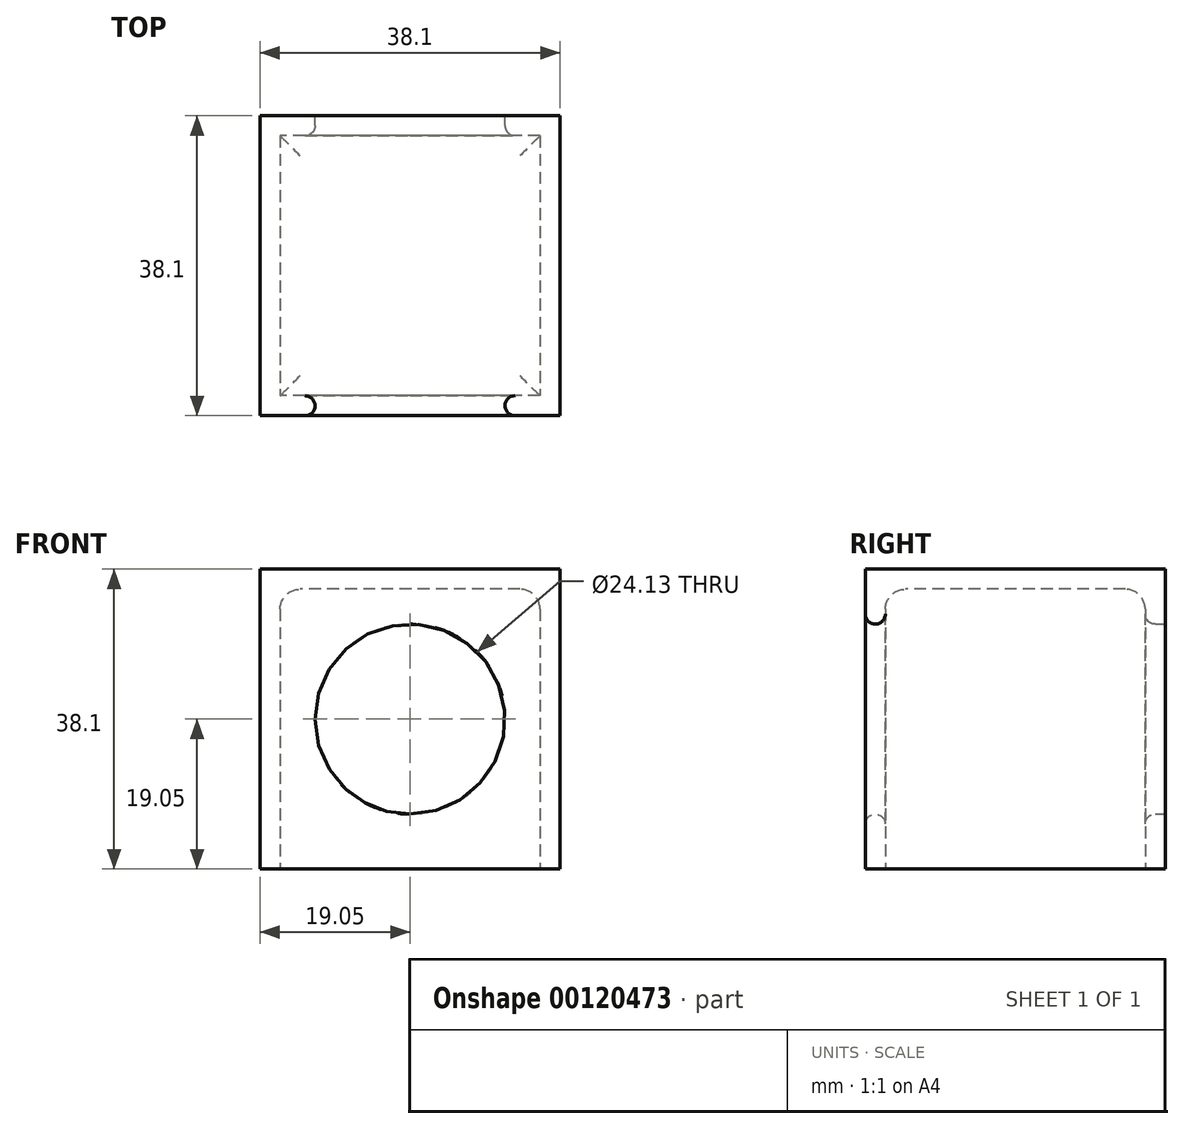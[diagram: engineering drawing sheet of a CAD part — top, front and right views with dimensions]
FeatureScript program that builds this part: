
annotation { "Feature Type Name" : "Feature", "Feature Type Description" : "" }
export const myFeature = defineFeature(function(context is Context, id is Id, definition is map)
    precondition{}
    {
        {
            var Q0;
            Q0=qCreatedBy(makeId("Top.planeOp"),FACE);
            var sketch = newSketch(context, id + "F0", { "sketchPlane" : qUnion([Q0])});
            skLineSegment(sketch, "E0.bottom", {"start": v(0, 0) * mm, "end": v(38.1, 0) * mm});
            skLineSegment(sketch, "E0.top", {"start": v(0, -38.1) * mm, "end": v(38.1, -38.1) * mm});
            skLineSegment(sketch, "E0.left", {"start": v(0, 0) * mm, "end": v(0, -38.1) * mm});
            skLineSegment(sketch, "E0.right", {"start": v(38.1, 0) * mm, "end": v(38.1, -38.1) * mm});
            skSolve(sketch);
        }
        {
            var Q0;
            Q0=makeQuery(id+"F0.imprint","IMPRINT",FACE,{"disambiguationData":[TD([[makeQuery(id+"F0.imprint","IMPRINT",EDGE,{"derivedFrom":sQuery(id+"F0.wireOp",EDGE,"E0.bottom")}),-1.0]])]});
            extrude(context, id + "F1", {"entities" : qUnion([Q0]), "depth" : 38.1 * mm});
        }
        {
            var Q0;
            Q0=makeQuery(id+"F1.opExtrude","CAP_FACE",FACE,{"disambiguationData":[OSD([sQuery(id+"F0.wireOp",EDGE,"E0.bottom"),sQuery(id+"F0.wireOp",EDGE,"E0.top"),sQuery(id+"F0.wireOp",EDGE,"E0.left"),sQuery(id+"F0.wireOp",EDGE,"E0.right")])],"isStart":true});
            var sketch = newSketch(context, id + "F2", { "sketchPlane" : qUnion([Q0])});
            skLineSegment(sketch, "E1.bottom", {"start": v(38.1, 0) * mm, "end": v(35.56, 0) * mm});
            skLineSegment(sketch, "E1.top", {"start": v(38.1, 2.54) * mm, "end": v(35.56, 2.54) * mm});
            skLineSegment(sketch, "E1.left", {"start": v(38.1, 0) * mm, "end": v(38.1, 2.54) * mm});
            skLineSegment(sketch, "E1.right", {"start": v(35.56, 0) * mm, "end": v(35.56, 2.54) * mm});
            skLineSegment(sketch, "E2.bottom", {"start": v(35.56, 2.54) * mm, "end": v(2.54, 2.54) * mm});
            skLineSegment(sketch, "E2.top", {"start": v(35.56, 35.56) * mm, "end": v(2.54, 35.56) * mm});
            skLineSegment(sketch, "E2.left", {"start": v(35.56, 2.54) * mm, "end": v(35.56, 35.56) * mm});
            skLineSegment(sketch, "E2.right", {"start": v(2.54, 2.54) * mm, "end": v(2.54, 35.56) * mm});
            skSolve(sketch);
        }
        {
            var Q0;
            Q0=makeQuery(id+"F2.imprint","IMPRINT",FACE,{"disambiguationData":[TD([[makeQuery(id+"F2.imprint","IMPRINT",EDGE,{"derivedFrom":sQuery(id+"F2.wireOp",EDGE,"E2.bottom")}),-1.0]])]});
            extrude(context, id + "F3", {"entities" : qUnion([Q0]), "operationType" : NewBodyOperationType.REMOVE, "oppositeDirection" : true, "depth" : 35.56 * mm});
        }
        {
            var Q0;
            Q0=makeQuery(id+"F3.boolean.opBoolean","COPY",EDGE,{"derivedFrom":makeQuery(id+"F3.opExtrude","CAP_EDGE",EDGE,{"disambiguationData":[OSD([sQuery(id+"F2.wireOp",EDGE,"E2.top")])],"isStart":false})});
            var Q1;
            Q1=makeQuery(id+"F3.boolean.opBoolean","COPY",EDGE,{"derivedFrom":makeQuery(id+"F3.opExtrude","CAP_EDGE",EDGE,{"disambiguationData":[OSD([sQuery(id+"F2.wireOp",EDGE,"E2.right")])],"isStart":false})});
            var Q2;
            Q2=makeQuery(id+"F3.boolean.opBoolean","COPY",EDGE,{"derivedFrom":makeQuery(id+"F3.opExtrude","CAP_EDGE",EDGE,{"disambiguationData":[OSD([sQuery(id+"F2.wireOp",EDGE,"E2.left")])],"isStart":false})});
            var Q3;
            Q3=makeQuery(id+"F3.boolean.opBoolean","COPY",EDGE,{"derivedFrom":makeQuery(id+"F3.opExtrude","CAP_EDGE",EDGE,{"disambiguationData":[OSD([sQuery(id+"F2.wireOp",EDGE,"E2.bottom")])],"isStart":false})});
            fillet(context, id + "F4", {"entities" : qUnion([Q0, Q1, Q2, Q3]), "radius" : 2.54 * mm, "tangentPropagation" : true, "allowEdgeOverflow" : false});
        }
        {
            var Q0;
            Q0=makeQuery(id+"F1.opExtrude","SWEPT_FACE",FACE,{"disambiguationData":[OSD([sQuery(id+"F0.wireOp",EDGE,"E0.bottom")])]});
            var sketch = newSketch(context, id + "F5", { "sketchPlane" : qUnion([Q0])});
            skCircle(sketch, "E3", {"center": v(-19.05, 19.05) * mm, "radius": 12.07 * mm});
            skSolve(sketch);
        }
        {
            var Q0;
            Q0 = qSketchRegion(id + "F5", true);
            extrude(context, id + "F6", {"entities" : qUnion([Q0]), "operationType" : NewBodyOperationType.REMOVE, "endBound" : BoundingType.THROUGH_ALL, "oppositeDirection" : true, "depth" : 25.4 * mm});
        }
        {
            var Q0;
            Q0=makeQuery(id+"F6.boolean.opBoolean","COPY",EDGE,{"derivedFrom":makeQuery(id+"F6.opExtrude","CAP_EDGE",EDGE,{"disambiguationData":[OSD([sQuery(id+"F5.wireOp",EDGE,"E3")])],"isStart":true})});
            var Q1;
            Q1=makeQuery(id+"F6.boolean.opBoolean","INTERSECT",EDGE,{"derivedFrom":[makeQuery(id+"F3.boolean.opBoolean","COPY",FACE,{"derivedFrom":makeQuery(id+"F3.opExtrude","SWEPT_FACE",FACE,{"disambiguationData":[OSD([sQuery(id+"F2.wireOp",EDGE,"E2.bottom")])]})}),makeQuery(id+"F6.opExtrude","SWEPT_FACE",FACE,{"disambiguationData":[OSD([sQuery(id+"F5.wireOp",EDGE,"E3")])]})]});
            var Q2;
            Q2=makeQuery(id+"F6.boolean.opBoolean","INTERSECT",EDGE,{"derivedFrom":[makeQuery(id+"F3.boolean.opBoolean","COPY",FACE,{"derivedFrom":makeQuery(id+"F3.opExtrude","SWEPT_FACE",FACE,{"disambiguationData":[OSD([sQuery(id+"F2.wireOp",EDGE,"E2.top")])]})}),makeQuery(id+"F6.opExtrude","SWEPT_FACE",FACE,{"disambiguationData":[OSD([sQuery(id+"F5.wireOp",EDGE,"E3")])]})]});
            var Q3;
            Q3=makeQuery(id+"F6.boolean.opBoolean","INTERSECT",EDGE,{"derivedFrom":[makeQuery(id+"F1.opExtrude","SWEPT_FACE",FACE,{"disambiguationData":[OSD([sQuery(id+"F0.wireOp",EDGE,"E0.top")])]}),makeQuery(id+"F6.opExtrude","SWEPT_FACE",FACE,{"disambiguationData":[OSD([sQuery(id+"F5.wireOp",EDGE,"E3")])]})]});
            fillet(context, id + "F7", {"entities" : qUnion([Q0, Q1, Q2, Q3]), "radius" : 1.27 * mm, "tangentPropagation" : true, "allowEdgeOverflow" : false});
        }
    });
